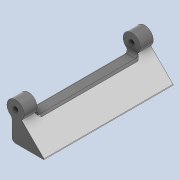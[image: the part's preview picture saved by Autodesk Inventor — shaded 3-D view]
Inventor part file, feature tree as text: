
AUTODESK INVENTOR PART (.ipt)
format: ipt  version: 2020.4 (Build 244396000, 396)  size: 258,560 bytes
history: native  units: mm
features: extrude x3, sketch x3, plane x2, fillet x2, projected_geometry x2, mirror x1
ambient origin geometry x8: Origin, YZ Plane, XZ Plane, XY Plane, X Axis, Y Axis, Z Axis, Center Point
bodies: Solid1 (feature_tree)
feature tree (13):
  extrude  "Extrusion1"  Depth=2.0mm
  plane  "Work Plane1"
  fillet  "Fillet1"  Radius=17.0mm
  extrude  "Extrusion3"  TaperAngle=45.0deg  [1 undecoded]
  extrude  "Extrusion4"  Depth=3.0mm
  fillet  "Fillet2"  Radius=3.0mm
  mirror  "Mirror2"
  plane  "Work Plane2"
  sketch  "Sketch1"  dims[d0=3.0mm d1=2.0mm d2=17.0mm]
  sketch  "Sketch3"  dims[d3=10.0mm d4=45.0deg]
  projected_geometry  "Projected Loop1"
  sketch  "Sketch4"  dims[d5=0.5mm d6=3.0mm d7=3.0mm d8=3.5mm d9=10.0mm d10=3.5mm d11=5.5mm d12=7.5mm d13=0.0mm d18=3.0mm d19=45.0deg d20=1.5mm d21=0.35mm d22=0.0mm d23=12.0mm d24=30.0mm d25=0.0mm d26=22.68928mm d27=8.0mm d28=10.0mm d29=0.0mm d30=2.0mm d31=1.0mm d40=-6.0mm d45=0.5mm d46=0.872665mm d47=0.5mm d48=0.872665mm]
  projected_geometry  "Projected Loop2"
note: 1 required parameter value undecoded (feature->parameter linkage not recoverable at this tier; creation-order binding heuristic only, values carry confidence <= 0.55)
